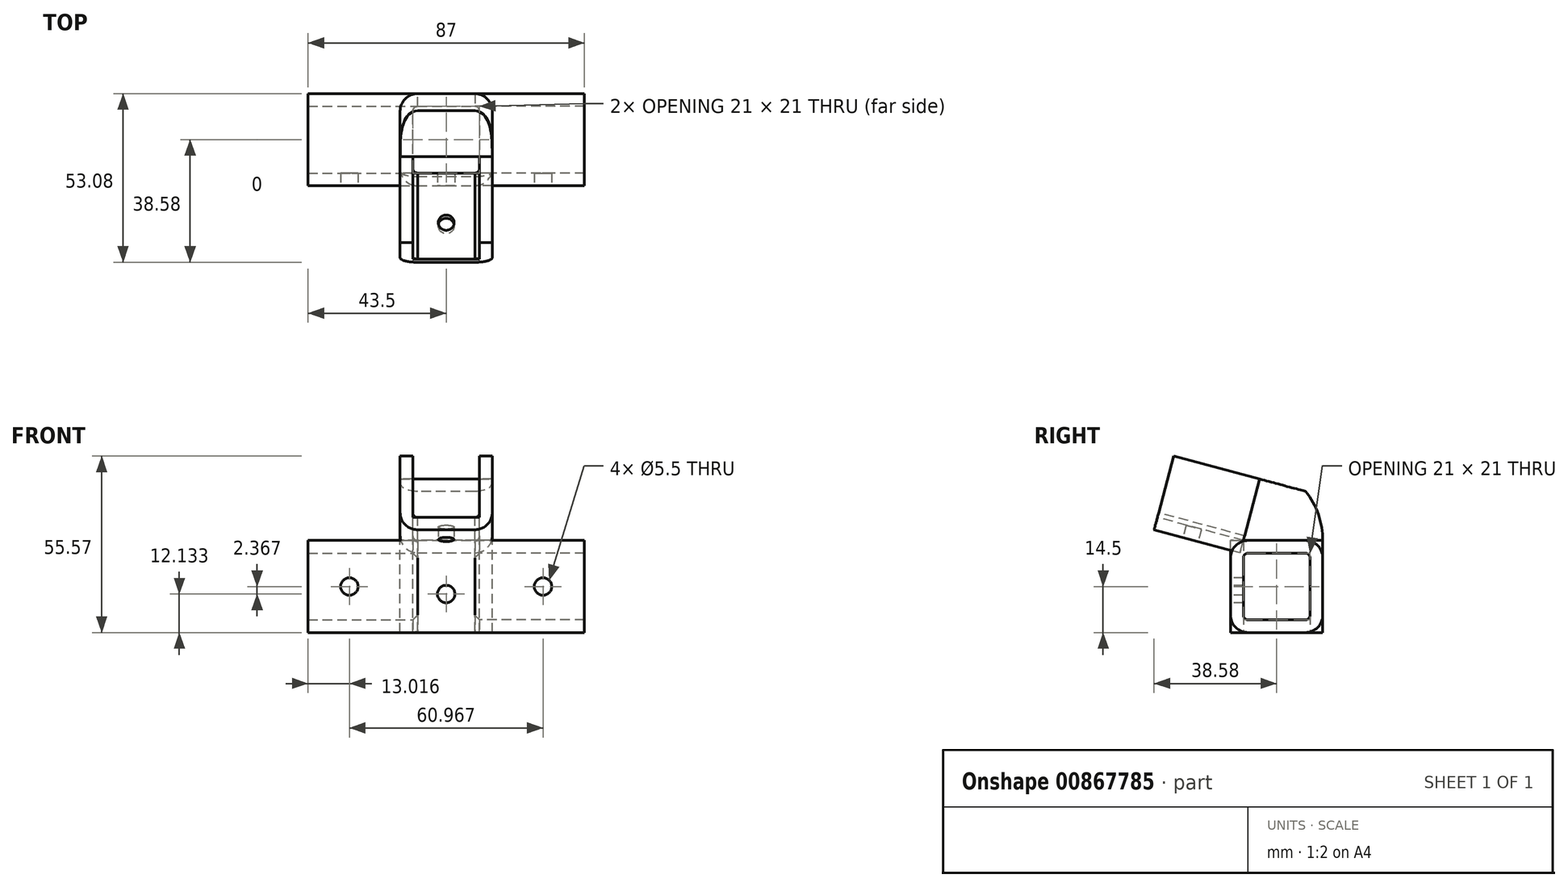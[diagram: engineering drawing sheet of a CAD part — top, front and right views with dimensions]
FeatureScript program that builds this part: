
annotation { "Feature Type Name" : "Feature", "Feature Type Description" : "" }
export const myFeature = defineFeature(function(context is Context, id is Id, definition is map)
    precondition{}
    {
        {
            var Q0;
            Q0=qCreatedBy(makeId("Top.planeOp"),FACE);
            var sketch = newSketch(context, id + "F0", { "sketchPlane" : qUnion([Q0])});
            skLineSegment(sketch, "E0.bottom", {"start": v(1.5, 0) * mm, "end": v(19.5, 0) * mm});
            skLineSegment(sketch, "E0.top", {"start": v(1.5, 21) * mm, "end": v(19.5, 21) * mm});
            skLineSegment(sketch, "E0.left", {"start": v(0, 1.5) * mm, "end": v(0, 19.5) * mm});
            skLineSegment(sketch, "E0.right", {"start": v(21, 1.5) * mm, "end": v(21, 19.5) * mm});
            skPoint(sketch, "E1.visualSharp", {"position": v(21, 21) * mm});
            skArc(sketch, "E1.filletArc", {"start": v(21, 19.5) * mm, "mid": v(20.56, 20.56) * mm, "end": v(19.5, 21) * mm});
            skPoint(sketch, "E2.visualSharp", {"position": v(21, 0) * mm});
            skArc(sketch, "E2.filletArc", {"start": v(19.5, 0) * mm, "mid": v(20.56, 0.44) * mm, "end": v(21, 1.5) * mm});
            skPoint(sketch, "E3.visualSharp", {"position": v(0, 0) * mm});
            skArc(sketch, "E3.filletArc", {"start": v(0, 1.5) * mm, "mid": v(0.44, 0.44) * mm, "end": v(1.5, 0) * mm});
            skPoint(sketch, "E4.visualSharp", {"position": v(0, 21) * mm});
            skArc(sketch, "E4.filletArc", {"start": v(1.5, 21) * mm, "mid": v(0.44, 20.56) * mm, "end": v(0, 19.5) * mm});
            skArc(sketch, "E5.0", {"start": v(19.5, -4) * mm, "mid": v(23.39, -2.39) * mm, "end": v(25, 1.5) * mm});
            skLineSegment(sketch, "E5.1", {"start": v(1.5, -4) * mm, "end": v(19.5, -4) * mm});
            skLineSegment(sketch, "E5.2", {"start": v(25, 1.5) * mm, "end": v(25, 19.5) * mm});
            skArc(sketch, "E5.3", {"start": v(-4, 1.5) * mm, "mid": v(-2.39, -2.39) * mm, "end": v(1.5, -4) * mm});
            skArc(sketch, "E5.4", {"start": v(25, 19.5) * mm, "mid": v(23.39, 23.39) * mm, "end": v(19.5, 25) * mm});
            skLineSegment(sketch, "E5.5", {"start": v(1.5, 25) * mm, "end": v(19.5, 25) * mm});
            skArc(sketch, "E5.6", {"start": v(1.5, 25) * mm, "mid": v(-2.39, 23.39) * mm, "end": v(-4, 19.5) * mm});
            skLineSegment(sketch, "E5.7", {"start": v(-4, 1.5) * mm, "end": v(-4, 19.5) * mm});
            skSolve(sketch);
        }
        {
            var Q0;
            Q0=makeQuery(id+"F0.imprint","IMPRINT",FACE,{"disambiguationData":[TD([[makeQuery(id+"F0.imprint","IMPRINT",EDGE,{"derivedFrom":sQuery(id+"F0.wireOp",EDGE,"E0.bottom")}),-1.0]])]});
            extrude(context, id + "F1", {"entities" : qUnion([Q0]), "oppositeDirection" : true, "depth" : 29 * mm, "offsetDistance" : 25 * mm});
        }
        {
            var Q0;
            Q0=qCreatedBy(makeId("Right.planeOp"),FACE);
            var sketch = newSketch(context, id + "F2", { "sketchPlane" : qUnion([Q0])});
            skLineSegment(sketch, "E6", {"start": v(0, 0) * mm, "end": v(-27.05, 7.25) * mm});
            skLineSegment(sketch, "E7", {"start": v(-27.05, 7.25) * mm, "end": v(-21.87, 26.57) * mm});
            skLineSegment(sketch, "E8", {"start": v(-21.87, 26.57) * mm, "end": v(5.18, 19.32) * mm});
            skLineSegment(sketch, "E9", {"start": v(5.18, 19.32) * mm, "end": v(0, 0) * mm});
            skSolve(sketch);
        }
        {
            var Q0;
            Q0=makeQuery(id+"F2.imprint","IMPRINT",FACE,{"disambiguationData":[TD([[makeQuery(id+"F2.imprint","IMPRINT",EDGE,{"derivedFrom":sQuery(id+"F2.wireOp",EDGE,"E6")}),-1.0]])]});
            extrude(context, id + "F3", {"entities" : qUnion([Q0]), "depth" : 21 * mm, "offsetDistance" : 25 * mm});
        }
        {
            var Q0;
            Q0=makeQuery(id+"F3.opExtrude","SWEPT_FACE",FACE,{"disambiguationData":[OSD([sQuery(id+"F2.wireOp",EDGE,"E7")])]});
            var sketch = newSketch(context, id + "F4", { "sketchPlane" : qUnion([Q0])});
            skLineSegment(sketch, "E10", {"start": v(0, 20) * mm, "end": v(0, 1.5) * mm});
            skLineSegment(sketch, "E11", {"start": v(1.5, 0) * mm, "end": v(19.5, 0) * mm});
            skLineSegment(sketch, "E12", {"start": v(21, 1.5) * mm, "end": v(21, 20) * mm});
            skPoint(sketch, "E13.visualSharp", {"position": v(0, 0) * mm});
            skArc(sketch, "E13.filletArc", {"start": v(0, 1.5) * mm, "mid": v(0.44, 0.44) * mm, "end": v(1.5, 0) * mm});
            skPoint(sketch, "E14.visualSharp", {"position": v(21, 0) * mm});
            skArc(sketch, "E14.filletArc", {"start": v(19.5, 0) * mm, "mid": v(20.56, 0.44) * mm, "end": v(21, 1.5) * mm});
            skLineSegment(sketch, "E15.0", {"start": v(25, 1.5) * mm, "end": v(25, 20) * mm});
            skLineSegment(sketch, "E15.1", {"start": v(-4, 20) * mm, "end": v(-4, 1.5) * mm});
            skArc(sketch, "E15.2", {"start": v(-4, 1.5) * mm, "mid": v(-2.39, -2.39) * mm, "end": v(1.5, -4) * mm});
            skLineSegment(sketch, "E15.3", {"start": v(1.5, -4) * mm, "end": v(19.5, -4) * mm});
            skArc(sketch, "E15.4", {"start": v(19.5, -4) * mm, "mid": v(23.39, -2.39) * mm, "end": v(25, 1.5) * mm});
            skLineSegment(sketch, "E16", {"start": v(-4, 20) * mm, "end": v(0, 20) * mm});
            skLineSegment(sketch, "E17", {"start": v(21, 20) * mm, "end": v(25, 20) * mm});
            skSolve(sketch);
        }
        {
            var Q0;
            {var subQ0=sQuery(id+"F4.wireOp",EDGE,"E10");Q0=makeQuery(id+"F4.imprint","IMPRINT",FACE,{"disambiguationData":[TD([[makeQuery(id+"F4.imprint","IMPRINT",EDGE,{"derivedFrom":subQ0}),1.0]])]});}
            extrude(context, id + "F5", {"entities" : qUnion([Q0]), "oppositeDirection" : true, "depth" : 28 * mm, "offsetDistance" : 25 * mm});
        }
        {
            var Q0;
            Q0=makeQuery(id+"F5.opExtrude","CAP_FACE",FACE,{"disambiguationData":[OSD([sQuery(id+"F2.wireOp",EDGE,"E6"),sQuery(id+"F2.wireOp",EDGE,"E7"),sQuery(id+"F4.wireOp",EDGE,"E10"),sQuery(id+"F4.wireOp",EDGE,"E11"),sQuery(id+"F4.wireOp",EDGE,"E12"),sQuery(id+"F4.wireOp",EDGE,"E15.0"),sQuery(id+"F4.wireOp",EDGE,"E15.1"),sQuery(id+"F4.wireOp",EDGE,"E15.2"),sQuery(id+"F4.wireOp",EDGE,"E15.3"),sQuery(id+"F4.wireOp",EDGE,"E15.4"),sQuery(id+"F4.wireOp",EDGE,"E16"),sQuery(id+"F4.wireOp",EDGE,"E17")])],"isStart":true});
            var sketch = newSketch(context, id + "F6", { "sketchPlane" : qUnion([Q0])});
            skLineSegment(sketch, "E18.bottom", {"start": v(0, 20) * mm, "end": v(21, 20) * mm});
            skLineSegment(sketch, "E18.top", {"start": v(1.5, 0) * mm, "end": v(19.5, 0) * mm});
            skLineSegment(sketch, "E18.left", {"start": v(0, 20) * mm, "end": v(0, 1.5) * mm});
            skLineSegment(sketch, "E18.right", {"start": v(21, 20) * mm, "end": v(21, 1.5) * mm});
            skPoint(sketch, "E19.visualSharp", {"position": v(0, 0) * mm});
            skArc(sketch, "E19.filletArc", {"start": v(0, 1.5) * mm, "mid": v(0.44, 0.44) * mm, "end": v(1.5, 0) * mm});
            skPoint(sketch, "E20.visualSharp", {"position": v(21, 0) * mm});
            skArc(sketch, "E20.filletArc", {"start": v(19.5, 0) * mm, "mid": v(20.56, 0.44) * mm, "end": v(21, 1.5) * mm});
            skSolve(sketch);
        }
        {
            var Q0;
            Q0=makeQuery(id+"F6.imprint","IMPRINT",FACE,{"disambiguationData":[TD([[makeQuery(id+"F6.imprint","IMPRINT",EDGE,{"derivedFrom":sQuery(id+"F6.wireOp",EDGE,"E18.bottom")}),-1.0]])]});
            extrude(context, id + "F7", {"entities" : qUnion([Q0]), "operationType" : NewBodyOperationType.REMOVE, "oppositeDirection" : true, "depth" : 28 * mm, "offsetDistance" : 25 * mm});
        }
        {
            var Q0;
            Q0=makeQuery(id+"F1.opExtrude","CAP_FACE",FACE,{"disambiguationData":[OSD([sQuery(id+"F0.wireOp",EDGE,"E0.bottom"),sQuery(id+"F0.wireOp",EDGE,"E0.top"),sQuery(id+"F0.wireOp",EDGE,"E0.left"),sQuery(id+"F0.wireOp",EDGE,"E0.right"),sQuery(id+"F0.wireOp",EDGE,"E1.filletArc"),sQuery(id+"F0.wireOp",EDGE,"E2.filletArc"),sQuery(id+"F0.wireOp",EDGE,"E3.filletArc"),sQuery(id+"F0.wireOp",EDGE,"E4.filletArc"),sQuery(id+"F0.wireOp",EDGE,"E5.0"),sQuery(id+"F0.wireOp",EDGE,"E5.1"),sQuery(id+"F0.wireOp",EDGE,"E5.2"),sQuery(id+"F0.wireOp",EDGE,"E5.3"),sQuery(id+"F0.wireOp",EDGE,"E5.4"),sQuery(id+"F0.wireOp",EDGE,"E5.5"),sQuery(id+"F0.wireOp",EDGE,"E5.6"),sQuery(id+"F0.wireOp",EDGE,"E5.7")])],"isStart":true});
            var sketch = newSketch(context, id + "F8", { "sketchPlane" : qUnion([Q0])});
            skLineSegment(sketch, "E21.bottom", {"start": v(1.5, 21) * mm, "end": v(19.5, 21) * mm});
            skLineSegment(sketch, "E21.top", {"start": v(1.5, 0) * mm, "end": v(19.5, 0) * mm});
            skLineSegment(sketch, "E21.left", {"start": v(0, 19.5) * mm, "end": v(0, 1.5) * mm});
            skLineSegment(sketch, "E21.right", {"start": v(21, 19.5) * mm, "end": v(21, 1.5) * mm});
            skPoint(sketch, "E22.visualSharp", {"position": v(21, 21) * mm});
            skArc(sketch, "E22.filletArc", {"start": v(21, 19.5) * mm, "mid": v(20.56, 20.56) * mm, "end": v(19.5, 21) * mm});
            skPoint(sketch, "E23.visualSharp", {"position": v(0, 21) * mm});
            skArc(sketch, "E23.filletArc", {"start": v(1.5, 21) * mm, "mid": v(0.44, 20.56) * mm, "end": v(0, 19.5) * mm});
            skPoint(sketch, "E24.visualSharp", {"position": v(0, 0) * mm});
            skArc(sketch, "E24.filletArc", {"start": v(0, 1.5) * mm, "mid": v(0.44, 0.44) * mm, "end": v(1.5, 0) * mm});
            skPoint(sketch, "E25.visualSharp", {"position": v(21, 0) * mm});
            skArc(sketch, "E25.filletArc", {"start": v(19.5, 0) * mm, "mid": v(20.56, 0.44) * mm, "end": v(21, 1.5) * mm});
            skArc(sketch, "E26.0", {"start": v(19.5, -4) * mm, "mid": v(23.39, -2.39) * mm, "end": v(25, 1.5) * mm});
            skLineSegment(sketch, "E26.1", {"start": v(25, 19.5) * mm, "end": v(25, 1.5) * mm});
            skArc(sketch, "E26.2", {"start": v(25, 19.5) * mm, "mid": v(23.39, 23.39) * mm, "end": v(19.5, 25) * mm});
            skArc(sketch, "E26.3", {"start": v(-4, 1.5) * mm, "mid": v(-2.39, -2.39) * mm, "end": v(1.5, -4) * mm});
            skLineSegment(sketch, "E26.4", {"start": v(-4, 19.5) * mm, "end": v(-4, 1.5) * mm});
            skArc(sketch, "E26.5", {"start": v(1.5, 25) * mm, "mid": v(-2.39, 23.39) * mm, "end": v(-4, 19.5) * mm});
            skLineSegment(sketch, "E26.6", {"start": v(1.5, 25) * mm, "end": v(19.5, 25) * mm});
            skLineSegment(sketch, "E27", {"start": v(24.8, 0) * mm, "end": v(-3.8, 0) * mm});
            skSolve(sketch);
        }
        {
            var Q0;
            Q0=makeQuery(id+"F8.imprint","IMPRINT",FACE,{"disambiguationData":[TD([[makeQuery(id+"F8.imprint","IMPRINT",EDGE,{"derivedFrom":sQuery(id+"F8.wireOp",EDGE,"E21.bottom")}),1.0]])]});
            var Q1;
            Q1=makeQuery(id+"F8.imprint","IMPRINT",FACE,{"disambiguationData":[TD([[makeQuery(id+"F8.imprint","IMPRINT",EDGE,{"derivedFrom":sQuery(id+"F8.wireOp",EDGE,"E21.bottom")}),-1.0]])]});
            var Q2;
            Q2=sQuery(id+"F8.wireOp",EDGE,"E21.top");
            revolve(context, id + "F9", {"surfaceOperationType" : NewSurfaceOperationType.NEW, "entities" : qUnion([Q0, Q1]), "axis" : qUnion([Q2]), "revolveType" : RevolveType.ONE_DIRECTION, "angle" : 75 * degree});
        }
        {
            var Q0;
            Q0=makeQuery(id+"F9.opRevolve","SWEPT_FACE",FACE,{"disambiguationData":[OSD([sQuery(id+"F8.wireOp",EDGE,"E26.4")])]});
            var sketch = newSketch(context, id + "F10", { "sketchPlane" : qUnion([Q0])});
            skLineSegment(sketch, "E28", {"start": v(-5.05, 18.84) * mm, "end": v(-5.18, 19.32) * mm});
            skLineSegment(sketch, "E29", {"start": v(-5.18, 19.32) * mm, "end": v(-21.6, 14.92) * mm});
            skLineSegment(sketch, "E30", {"start": v(-21.6, 14.92) * mm, "end": v(-23.5, 23.3) * mm});
            skLineSegment(sketch, "E31", {"start": v(-23.5, 23.3) * mm, "end": v(-5.18, 24.55) * mm});
            skLineSegment(sketch, "E32", {"start": v(-5.18, 24.55) * mm, "end": v(-5.18, 19.32) * mm});
            skSolve(sketch);
        }
        {
            var Q0;
            Q0=makeQuery(id+"F10.imprint","IMPRINT",FACE,{"disambiguationData":[TD([[makeQuery(id+"F10.imprint","IMPRINT",EDGE,{"derivedFrom":sQuery(id+"F10.wireOp",EDGE,"E29")}),-1.0]])]});
            extrude(context, id + "F11", {"entities" : qUnion([Q0]), "operationType" : NewBodyOperationType.REMOVE, "oppositeDirection" : true, "depth" : 43.3 * mm, "offsetDistance" : 25 * mm});
        }
        {
            var Q0;
            Q0=makeQuery(id+"F1.opExtrude","SWEPT_FACE",FACE,{"disambiguationData":[OSD([sQuery(id+"F0.wireOp",EDGE,"E5.1")])]});
            var sketch = newSketch(context, id + "F12", { "sketchPlane" : qUnion([Q0])});
            skCircle(sketch, "E33", {"center": v(10.5, -16.87) * mm, "radius": 2.75 * mm});
            skPoint(sketch, "E33.centerSnap0", {"position": v(10.5, -29) * mm});
            skSolve(sketch);
        }
        {
            var Q0;
            Q0=makeQuery(id+"F12.imprint","IMPRINT",FACE,{"disambiguationData":[TD([[makeQuery(id+"F12.imprint","IMPRINT",EDGE,{"derivedFrom":sQuery(id+"F12.wireOp",EDGE,"E33")}),1.0]])]});
            extrude(context, id + "F13", {"entities" : qUnion([Q0]), "operationType" : NewBodyOperationType.REMOVE, "oppositeDirection" : true, "depth" : 5 * mm, "offsetDistance" : 25 * mm});
        }
        {
            var Q0;
            Q0=makeQuery(id+"F5.opExtrude","SWEPT_FACE",FACE,{"disambiguationData":[OSD([sQuery(id+"F4.wireOp",EDGE,"E15.3")])]});
            var sketch = newSketch(context, id + "F14", { "sketchPlane" : qUnion([Q0])});
            skCircle(sketch, "E34", {"center": v(10.5, 16.15) * mm, "radius": 2.5 * mm});
            skPoint(sketch, "E34.centerSnap0", {"position": v(10.5, 28) * mm});
            skSolve(sketch);
        }
        {
            var Q0;
            Q0=makeQuery(id+"F14.imprint","IMPRINT",FACE,{"disambiguationData":[TD([[makeQuery(id+"F14.imprint","IMPRINT",EDGE,{"derivedFrom":sQuery(id+"F14.wireOp",EDGE,"E34")}),1.0]])]});
            extrude(context, id + "F15", {"entities" : qUnion([Q0]), "operationType" : NewBodyOperationType.REMOVE, "oppositeDirection" : true, "depth" : 5 * mm, "offsetDistance" : 25 * mm});
        }
        {
            var Q0;
            Q0=makeQuery(id+"F1.opExtrude","SWEPT_FACE",FACE,{"disambiguationData":[OSD([sQuery(id+"F0.wireOp",EDGE,"E5.2")])]});
            var sketch = newSketch(context, id + "F16", { "sketchPlane" : qUnion([Q0])});
            skLineSegment(sketch, "E35", {"start": v(1.5, -29) * mm, "end": v(-4, -29) * mm});
            skLineSegment(sketch, "E36", {"start": v(-4, -29) * mm, "end": v(-4, -29) * mm});
            skLineSegment(sketch, "E37.bottom", {"start": v(1.5, -29) * mm, "end": v(19.5, -29) * mm});
            skLineSegment(sketch, "E37.top", {"start": v(1.5, 0) * mm, "end": v(19.5, 0) * mm});
            skLineSegment(sketch, "E37.left", {"start": v(-4, -23.5) * mm, "end": v(-4, -5.5) * mm});
            skLineSegment(sketch, "E37.right", {"start": v(25, -23.5) * mm, "end": v(25, -5.5) * mm});
            skPoint(sketch, "E38.visualSharp", {"position": v(-4, 0) * mm});
            skArc(sketch, "E38.filletArc", {"start": v(1.5, 0) * mm, "mid": v(-2.39, -1.61) * mm, "end": v(-4, -5.5) * mm});
            skPoint(sketch, "E39.visualSharp", {"position": v(25, 0) * mm});
            skArc(sketch, "E39.filletArc", {"start": v(25, -5.5) * mm, "mid": v(23.39, -1.61) * mm, "end": v(19.5, 0) * mm});
            skPoint(sketch, "E40.visualSharp", {"position": v(25, -29) * mm});
            skArc(sketch, "E40.filletArc", {"start": v(19.5, -29) * mm, "mid": v(23.39, -27.39) * mm, "end": v(25, -23.5) * mm});
            skPoint(sketch, "E41.visualSharp", {"position": v(-4, -29) * mm});
            skArc(sketch, "E41.filletArc", {"start": v(-4, -23.5) * mm, "mid": v(-2.39, -27.39) * mm, "end": v(1.5, -29) * mm});
            skLineSegment(sketch, "E42.0", {"start": v(1.5, -4) * mm, "end": v(19.5, -4) * mm});
            skArc(sketch, "E42.1", {"start": v(21, -5.5) * mm, "mid": v(20.56, -4.44) * mm, "end": v(19.5, -4) * mm});
            skArc(sketch, "E42.2", {"start": v(1.5, -4) * mm, "mid": v(0.44, -4.44) * mm, "end": v(0, -5.5) * mm});
            skLineSegment(sketch, "E42.3", {"start": v(21, -23.5) * mm, "end": v(21, -5.5) * mm});
            skLineSegment(sketch, "E42.4", {"start": v(0, -23.5) * mm, "end": v(0, -5.5) * mm});
            skArc(sketch, "E42.5", {"start": v(0, -23.5) * mm, "mid": v(0.44, -24.56) * mm, "end": v(1.5, -25) * mm});
            skLineSegment(sketch, "E42.6", {"start": v(1.5, -25) * mm, "end": v(19.5, -25) * mm});
            skArc(sketch, "E42.7", {"start": v(19.5, -25) * mm, "mid": v(20.56, -24.56) * mm, "end": v(21, -23.5) * mm});
            skSolve(sketch);
        }
        {
            var Q0;
            Q0=makeQuery(id+"F16.imprint","IMPRINT",FACE,{"disambiguationData":[TD([[makeQuery(id+"F16.imprint","IMPRINT",EDGE,{"derivedFrom":sQuery(id+"F16.wireOp",EDGE,"E37.top")}),-1.0]])]});
            var Q1;
            {var subQ0=sQuery(id+"F16.wireOp",EDGE,"E37.bottom");Q1=makeQuery(id+"F16.imprint","IMPRINT",FACE,{"disambiguationData":[TD([[makeQuery(id+"F16.imprint","IMPRINT",EDGE,{"derivedFrom":subQ0}),1.0]])]});}
            var Q2;
            {var subQ0=sQuery(id+"F16.wireOp",EDGE,"E42.0");Q2=makeQuery(id+"F16.imprint","IMPRINT",FACE,{"disambiguationData":[TD([[makeQuery(id+"F16.imprint","IMPRINT",EDGE,{"derivedFrom":subQ0}),1.0]])]});}
            var Q3;
            Q3=makeQuery(id+"F16.imprint","IMPRINT",FACE,{"disambiguationData":[TD([[makeQuery(id+"F16.imprint","IMPRINT",EDGE,{"derivedFrom":sQuery(id+"F16.wireOp",EDGE,"E37.left")}),-1.0]])]});
            var Q4;
            Q4=makeQuery(id+"F16.imprint","IMPRINT",FACE,{"disambiguationData":[TD([[makeQuery(id+"F16.imprint","IMPRINT",EDGE,{"derivedFrom":sQuery(id+"F16.wireOp",EDGE,"E37.right")}),1.0]])]});
            extrude(context, id + "F17", {"entities" : qUnion([Q0, Q1, Q2, Q3, Q4]), "endBound" : BoundingType.SYMMETRIC, "depth" : 11 * mm, "offsetDistance" : 25 * mm});
        }
        {
            var Q0;
            Q0=makeQuery(id+"F17.opExtrude","SWEPT_FACE",FACE,{"disambiguationData":[OSD([sQuery(id+"F16.wireOp",EDGE,"E37.bottom")])]});
            var sketch = newSketch(context, id + "F18", { "sketchPlane" : qUnion([Q0])});
            skLineSegment(sketch, "E43", {"start": v(19.5, 0) * mm, "end": v(19.5, -21) * mm});
            skLineSegment(sketch, "E44", {"start": v(19.5, -21) * mm, "end": v(19.5, -21) * mm});
            skLineSegment(sketch, "E45", {"start": v(21, -19.5) * mm, "end": v(21, -1.5) * mm});
            skLineSegment(sketch, "E46", {"start": v(19.5, 0) * mm, "end": v(19.5, 0) * mm});
            skPoint(sketch, "E47.visualSharp", {"position": v(21, -21) * mm});
            skArc(sketch, "E47.filletArc", {"start": v(19.5, -21) * mm, "mid": v(20.56, -20.56) * mm, "end": v(21, -19.5) * mm});
            skPoint(sketch, "E48.visualSharp", {"position": v(21, 0) * mm});
            skArc(sketch, "E48.filletArc", {"start": v(21, -1.5) * mm, "mid": v(20.56, -0.44) * mm, "end": v(19.5, 0) * mm});
            skSolve(sketch);
        }
        {
            var Q0;
            {var subQ3=sQuery(id+"F18.wireOp",EDGE,"E48.filletArc");Q0=makeQuery(id+"F18.imprint","IMPRINT",FACE,{"disambiguationData":[TD([[makeQuery(id+"F18.imprint","IMPRINT",EDGE,{"derivedFrom":subQ3}),1.0]])]});}
            var Q1;
            {var subQ7=sQuery(id+"F18.wireOp",EDGE,"E45");Q1=makeQuery(id+"F18.imprint","IMPRINT",FACE,{"disambiguationData":[TD([[makeQuery(id+"F18.imprint","IMPRINT",EDGE,{"derivedFrom":subQ7}),1.0]])]});}
            var Q2;
            {var subQ3=sQuery(id+"F18.wireOp",EDGE,"E47.filletArc");Q2=makeQuery(id+"F18.imprint","IMPRINT",FACE,{"disambiguationData":[TD([[makeQuery(id+"F18.imprint","IMPRINT",EDGE,{"derivedFrom":subQ3}),1.0]])]});}
            extrude(context, id + "F19", {"entities" : qUnion([Q0, Q1, Q2]), "operationType" : NewBodyOperationType.REMOVE, "oppositeDirection" : true, "depth" : 29 * mm, "offsetDistance" : 25 * mm});
        }
        {
            var Q0;
            Q0=makeQuery(id+"F17.opExtrude","CAP_FACE",FACE,{"disambiguationData":[OSD([sQuery(id+"F16.wireOp",EDGE,"E37.bottom"),sQuery(id+"F16.wireOp",EDGE,"E37.top"),sQuery(id+"F16.wireOp",EDGE,"E37.left"),sQuery(id+"F16.wireOp",EDGE,"E37.right"),sQuery(id+"F16.wireOp",EDGE,"E38.filletArc"),sQuery(id+"F16.wireOp",EDGE,"E39.filletArc"),sQuery(id+"F16.wireOp",EDGE,"E40.filletArc"),sQuery(id+"F16.wireOp",EDGE,"E41.filletArc"),sQuery(id+"F16.wireOp",EDGE,"E42.0"),sQuery(id+"F16.wireOp",EDGE,"E42.1"),sQuery(id+"F16.wireOp",EDGE,"E42.2"),sQuery(id+"F16.wireOp",EDGE,"E42.3"),sQuery(id+"F16.wireOp",EDGE,"E42.4"),sQuery(id+"F16.wireOp",EDGE,"E42.5"),sQuery(id+"F16.wireOp",EDGE,"E42.6"),sQuery(id+"F16.wireOp",EDGE,"E42.7")])],"isStart":false});
            var sketch = newSketch(context, id + "F20", { "sketchPlane" : qUnion([Q0])});
            skLineSegment(sketch, "E49", {"start": v(1.5, -25) * mm, "end": v(19.5, -25) * mm});
            skLineSegment(sketch, "E50", {"start": v(21, -23.5) * mm, "end": v(21, -5.5) * mm});
            skLineSegment(sketch, "E51", {"start": v(19.5, -4) * mm, "end": v(1.5, -4) * mm});
            skLineSegment(sketch, "E52", {"start": v(0, -5.5) * mm, "end": v(0, -23.5) * mm});
            skLineSegment(sketch, "E53", {"start": v(1.5, -25) * mm, "end": v(1.5, -25) * mm});
            skPoint(sketch, "E54.visualSharp", {"position": v(0, -4) * mm});
            skArc(sketch, "E54.filletArc", {"start": v(1.5, -4) * mm, "mid": v(0.44, -4.44) * mm, "end": v(0, -5.5) * mm});
            skPoint(sketch, "E55.visualSharp", {"position": v(21, -4) * mm});
            skArc(sketch, "E55.filletArc", {"start": v(21, -5.5) * mm, "mid": v(20.56, -4.44) * mm, "end": v(19.5, -4) * mm});
            skPoint(sketch, "E56.visualSharp", {"position": v(21, -25) * mm});
            skArc(sketch, "E56.filletArc", {"start": v(19.5, -25) * mm, "mid": v(20.56, -24.56) * mm, "end": v(21, -23.5) * mm});
            skPoint(sketch, "E57.visualSharp", {"position": v(0, -25) * mm});
            skArc(sketch, "E57.filletArc", {"start": v(0, -23.5) * mm, "mid": v(0.44, -24.56) * mm, "end": v(1.5, -25) * mm});
            skArc(sketch, "E58.0", {"start": v(25, -5.5) * mm, "mid": v(23.39, -1.61) * mm, "end": v(19.5, 0) * mm});
            skLineSegment(sketch, "E58.1", {"start": v(25, -23.5) * mm, "end": v(25, -5.5) * mm});
            skLineSegment(sketch, "E58.2", {"start": v(19.5, 0) * mm, "end": v(1.5, 0) * mm});
            skArc(sketch, "E58.3", {"start": v(19.5, -29) * mm, "mid": v(23.39, -27.39) * mm, "end": v(25, -23.5) * mm});
            skArc(sketch, "E58.4", {"start": v(1.5, 0) * mm, "mid": v(-2.39, -1.61) * mm, "end": v(-4, -5.5) * mm});
            skLineSegment(sketch, "E58.5", {"start": v(-4, -5.5) * mm, "end": v(-4, -23.5) * mm});
            skArc(sketch, "E58.6", {"start": v(-4, -23.5) * mm, "mid": v(-2.39, -27.39) * mm, "end": v(1.5, -29) * mm});
            skLineSegment(sketch, "E58.7", {"start": v(1.5, -29) * mm, "end": v(19.5, -29) * mm});
            skSolve(sketch);
        }
        {
            var Q0;
            Q0=makeQuery(id+"F20.imprint","IMPRINT",FACE,{"disambiguationData":[TD([[makeQuery(id+"F20.imprint","IMPRINT",EDGE,{"derivedFrom":sQuery(id+"F20.wireOp",EDGE,"E49")}),-1.0]])]});
            extrude(context, id + "F21", {"entities" : qUnion([Q0]), "operationType" : NewBodyOperationType.ADD, "depth" : 23.5 * mm, "offsetDistance" : 25 * mm});
        }
        {
            var Q0;
            Q0=makeQuery(id+"F21.boolean.opBoolean","MERGE",FACE,{"derivedFrom":[makeQuery(id+"F17.opExtrude","SWEPT_FACE",FACE,{"disambiguationData":[OSD([sQuery(id+"F16.wireOp",EDGE,"E37.left")])]}),makeQuery(id+"F21.opExtrude","SWEPT_FACE",FACE,{"disambiguationData":[OSD([sQuery(id+"F20.wireOp",EDGE,"E58.5")])]})]});
            var sketch = newSketch(context, id + "F22", { "sketchPlane" : qUnion([Q0])});
            skCircle(sketch, "E59", {"center": v(40.98, -14.5) * mm, "radius": 2.75 * mm});
            skPoint(sketch, "E59.centerSnap0", {"position": v(54, -14.5) * mm});
            skSolve(sketch);
        }
        {
            var Q0;
            Q0=makeQuery(id+"F22.imprint","IMPRINT",FACE,{"disambiguationData":[TD([[makeQuery(id+"F22.imprint","IMPRINT",EDGE,{"derivedFrom":sQuery(id+"F22.wireOp",EDGE,"E59")}),1.0]])]});
            extrude(context, id + "F23", {"entities" : qUnion([Q0]), "operationType" : NewBodyOperationType.REMOVE, "oppositeDirection" : true, "depth" : 15.2 * mm, "offsetDistance" : 25 * mm});
        }
        {
            var Q0;
            Q0=qCreatedBy(makeId("Right.planeOp"),FACE);
            cPlane(context, id + "F24", {"entities" : qUnion([Q0]), "cplaneType" : CPlaneType.OFFSET, "offset" : (21 / 2) * mm, "width" : 150 * mm, "height" : 150 * mm});
        }
        {
            var Q0;
            Q0=makeQuery(id+"F17.opExtrude","SWEPT_BODY",BODY,{"disambiguationData":[OSD([sQuery(id+"F16.wireOp",EDGE,"E37.bottom"),sQuery(id+"F16.wireOp",EDGE,"E37.top"),sQuery(id+"F16.wireOp",EDGE,"E37.left"),sQuery(id+"F16.wireOp",EDGE,"E37.right"),sQuery(id+"F16.wireOp",EDGE,"E38.filletArc"),sQuery(id+"F16.wireOp",EDGE,"E39.filletArc"),sQuery(id+"F16.wireOp",EDGE,"E40.filletArc"),sQuery(id+"F16.wireOp",EDGE,"E41.filletArc"),sQuery(id+"F16.wireOp",EDGE,"E42.0"),sQuery(id+"F16.wireOp",EDGE,"E42.1"),sQuery(id+"F16.wireOp",EDGE,"E42.2"),sQuery(id+"F16.wireOp",EDGE,"E42.3"),sQuery(id+"F16.wireOp",EDGE,"E42.4"),sQuery(id+"F16.wireOp",EDGE,"E42.5"),sQuery(id+"F16.wireOp",EDGE,"E42.6"),sQuery(id+"F16.wireOp",EDGE,"E42.7")])]});
            var Q1;
            Q1=makeQuery(id+"F1.opExtrude","SWEPT_BODY",BODY,{"disambiguationData":[OSD([sQuery(id+"F0.wireOp",EDGE,"E0.bottom"),sQuery(id+"F0.wireOp",EDGE,"E0.top"),sQuery(id+"F0.wireOp",EDGE,"E0.left"),sQuery(id+"F0.wireOp",EDGE,"E0.right"),sQuery(id+"F0.wireOp",EDGE,"E1.filletArc"),sQuery(id+"F0.wireOp",EDGE,"E2.filletArc"),sQuery(id+"F0.wireOp",EDGE,"E3.filletArc"),sQuery(id+"F0.wireOp",EDGE,"E4.filletArc"),sQuery(id+"F0.wireOp",EDGE,"E5.0"),sQuery(id+"F0.wireOp",EDGE,"E5.1"),sQuery(id+"F0.wireOp",EDGE,"E5.2"),sQuery(id+"F0.wireOp",EDGE,"E5.3"),sQuery(id+"F0.wireOp",EDGE,"E5.4"),sQuery(id+"F0.wireOp",EDGE,"E5.5"),sQuery(id+"F0.wireOp",EDGE,"E5.6"),sQuery(id+"F0.wireOp",EDGE,"E5.7")])]});
            var Q2;
            Q2=makeQuery(id+"F9.opRevolve","SWEPT_BODY",BODY,{"disambiguationData":[OSD([sQuery(id+"F8.wireOp",EDGE,"E21.top"),sQuery(id+"F8.wireOp",EDGE,"E26.0"),sQuery(id+"F8.wireOp",EDGE,"E26.1"),sQuery(id+"F8.wireOp",EDGE,"E26.2"),sQuery(id+"F8.wireOp",EDGE,"E26.3"),sQuery(id+"F8.wireOp",EDGE,"E26.4"),sQuery(id+"F8.wireOp",EDGE,"E26.5"),sQuery(id+"F8.wireOp",EDGE,"E26.6"),sQuery(id+"F8.wireOp",EDGE,"E27")])]});
            var Q3;
            Q3=qCreatedBy(id+"F24.planeOp",FACE);
            mirror(context, id + "F25", {"entities" : qUnion([Q0, Q1, Q2]), "mirrorPlane" : qUnion([Q3])});
        }
    });
